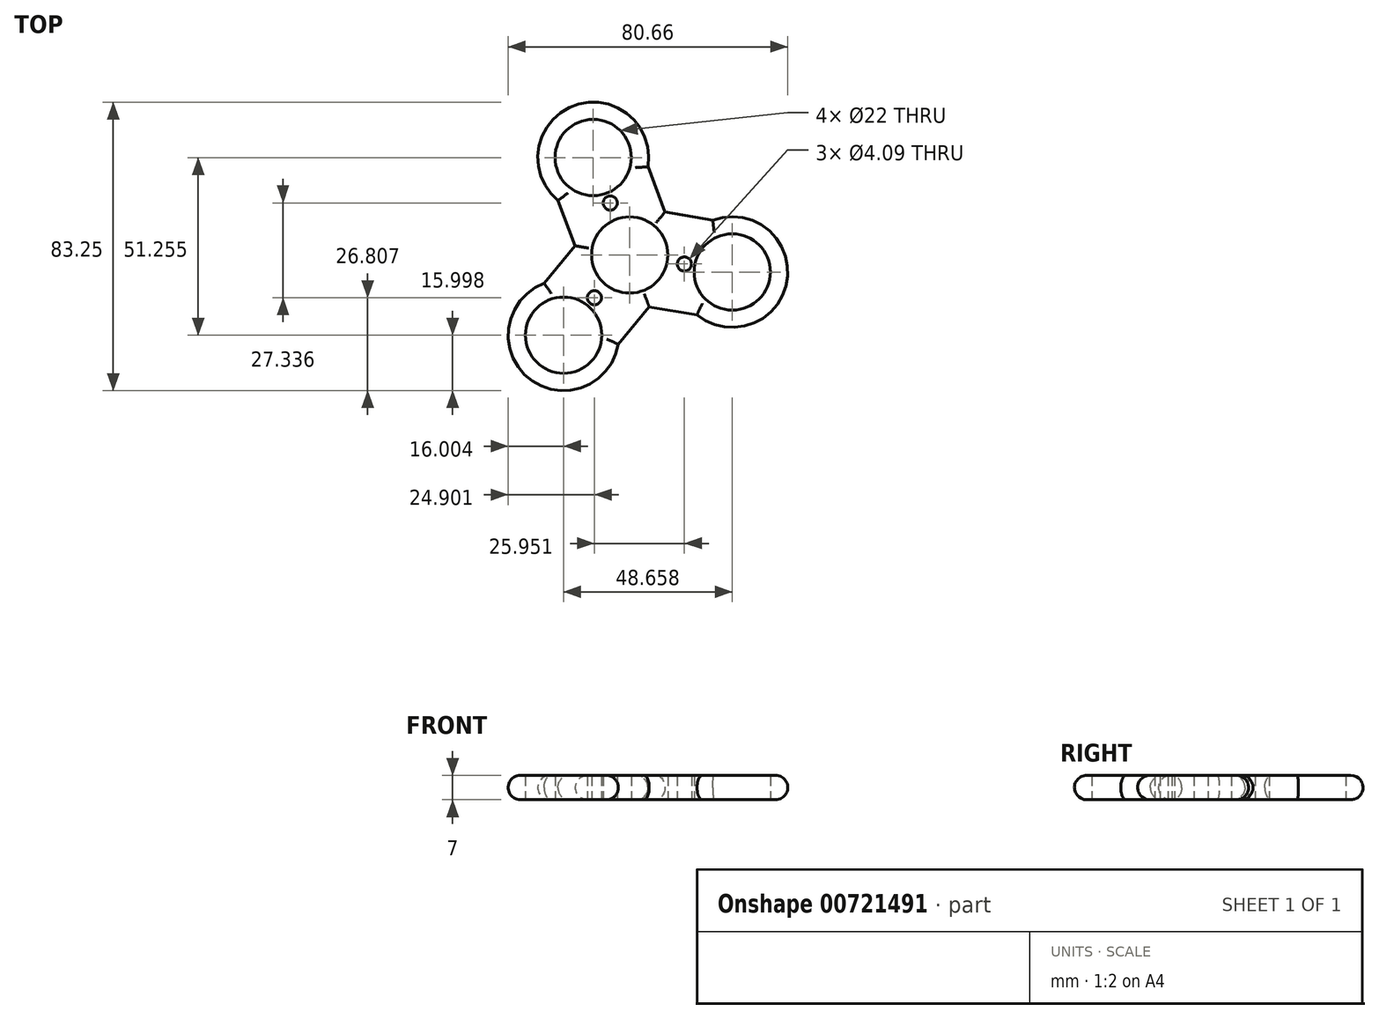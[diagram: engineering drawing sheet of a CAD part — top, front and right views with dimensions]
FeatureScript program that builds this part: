
annotation { "Feature Type Name" : "Feature", "Feature Type Description" : "" }
export const myFeature = defineFeature(function(context is Context, id is Id, definition is map)
    precondition{}
    {
        {
            var Q0;
            Q0=qCreatedBy(makeId("Top.planeOp"),FACE);
            var sketch = newSketch(context, id + "F0", { "sketchPlane" : qUnion([Q0])});
            skCircle(sketch, "E0", {"center": v(0, 0) * mm, "radius": 11 * mm});
            skLineSegment(sketch, "E1", {"start": v(0, 0) * mm, "end": v(-10.53, 28.1) * mm});
            skLineSegment(sketch, "E2", {"start": v(0, 0) * mm, "end": v(-19.07, -23.16) * mm});
            skLineSegment(sketch, "E3", {"start": v(0, 0) * mm, "end": v(29.6, -4.93) * mm});
            skCircle(sketch, "E4", {"center": v(-10.53, 28.1) * mm, "radius": 11 * mm});
            skCircle(sketch, "E5", {"center": v(29.6, -4.93) * mm, "radius": 11 * mm});
            skCircle(sketch, "E6", {"center": v(-19.07, -23.16) * mm, "radius": 11 * mm});
            skCircle(sketch, "E7", {"center": v(-10.53, 28.1) * mm, "radius": 16 * mm});
            skCircle(sketch, "E8", {"center": v(29.6, -4.93) * mm, "radius": 16 * mm});
            skCircle(sketch, "E9", {"center": v(-19.07, -23.16) * mm, "radius": 16 * mm});
            skCircle(sketch, "E10", {"center": v(0, 0) * mm, "radius": 16 * mm});
            skLineSegment(sketch, "E11", {"start": v(0, 0) * mm, "end": v(-15.78, 2.63) * mm, "construction": true});
            skLineSegment(sketch, "E12", {"start": v(0, 0) * mm, "end": v(10.17, 12.35) * mm, "construction": true});
            skLineSegment(sketch, "E13", {"start": v(-10.53, 28.1) * mm, "end": v(-20.7, 15.74) * mm, "construction": true});
            skLineSegment(sketch, "E14", {"start": v(-10.53, 28.1) * mm, "end": v(5.26, 25.46) * mm});
            skLineSegment(sketch, "E15", {"start": v(10.17, 12.35) * mm, "end": v(5.26, 25.46) * mm});
            skLineSegment(sketch, "E16", {"start": v(-15.78, 2.63) * mm, "end": v(-20.7, 15.74) * mm});
            skLineSegment(sketch, "E17.MirrorCS", {"start": v(5.61, -14.98) * mm, "end": v(19.42, -17.28) * mm});
            skLineSegment(sketch, "E18.MirrorCS", {"start": v(10.17, 12.35) * mm, "end": v(23.98, 10.05) * mm});
            skLineSegment(sketch, "E19.MirrorCS", {"start": v(-15.78, 2.63) * mm, "end": v(-24.68, -8.18) * mm});
            skLineSegment(sketch, "E20.MirrorCS", {"start": v(5.61, -14.98) * mm, "end": v(-3.28, -25.8) * mm});
            skCircle(sketch, "E21", {"center": v(-10.17, -12.35) * mm, "radius": 2.05 * mm});
            skCircle(sketch, "E22.MirrorC", {"center": v(-5.61, 14.98) * mm, "radius": 2.05 * mm});
            skCircle(sketch, "E23.MirrorC", {"center": v(15.78, -2.63) * mm, "radius": 2.05 * mm});
            skSolve(sketch);
        }
        {
            var Q0;
            Q0=makeQuery(id+"F0.imprint","IMPRINT",FACE,{"disambiguationData":[TD([[makeQuery(id+"F0.imprint","IMPRINT",EDGE,{"derivedFrom":sQuery(id+"F0.wireOp",EDGE,"E5")}),-1.0]])]});
            var Q1;
            Q1=makeQuery(id+"F0.imprint","IMPRINT",FACE,{"disambiguationData":[TD([[makeQuery(id+"F0.imprint","IMPRINT",EDGE,{"derivedFrom":sQuery(id+"F0.wireOp",EDGE,"E6")}),-1.0]])]});
            var Q2;
            {var subQ4=sQuery(id+"F0.wireOp",EDGE,"E2");var subQ5=sQuery(id+"F0.wireOp",EDGE,"E0");var subQ6=makeQuery(id+"F0.imprint","INTERSECT",VERTEX,{"derivedFrom":[subQ5,subQ4]});Q2=makeQuery(id+"F0.imprint","IMPRINT",FACE,{"disambiguationData":[TD([[makeQuery(id+"F0.imprint","IMPRINT",EDGE,{"disambiguationData":[TD([[subQ6,1.0]])],"derivedFrom":subQ5}),-1.0]])]});}
            var Q3;
            {var subQ2=sQuery(id+"F0.wireOp",EDGE,"E2");var subQ5=sQuery(id+"F0.wireOp",EDGE,"E0");var subQ8=makeQuery(id+"F0.imprint","INTERSECT",VERTEX,{"derivedFrom":[subQ5,subQ2]});Q3=makeQuery(id+"F0.imprint","IMPRINT",FACE,{"disambiguationData":[TD([[makeQuery(id+"F0.imprint","IMPRINT",EDGE,{"disambiguationData":[TD([[subQ8,-1.0]])],"derivedFrom":subQ5}),-1.0]])]});}
            var Q4;
            {var subQ0=sQuery(id+"F0.wireOp",EDGE,"E1");var subQ1=sQuery(id+"F0.wireOp",EDGE,"E0");var subQ2=makeQuery(id+"F0.imprint","INTERSECT",VERTEX,{"derivedFrom":[subQ1,subQ0]});Q4=makeQuery(id+"F0.imprint","IMPRINT",FACE,{"disambiguationData":[TD([[makeQuery(id+"F0.imprint","IMPRINT",EDGE,{"disambiguationData":[TD([[subQ2,1.0]])],"derivedFrom":subQ1}),-1.0]])]});}
            var Q5;
            {var subQ0=sQuery(id+"F0.wireOp",EDGE,"wNWGQW3L-Wg3f-4ug6-IvEM-VYyaZqjxjgMl");var subQ1=sQuery(id+"F0.wireOp",EDGE,"E20.MirrorCS");var subQ2=makeQuery(id+"F0.imprint","INTERSECT",VERTEX,{"disambiguationData":[OD(0.0)],"derivedFrom":[subQ1,subQ0]});Q5=makeQuery(id+"F0.imprint","IMPRINT",FACE,{"disambiguationData":[TD([[makeQuery(id+"F0.imprint","IMPRINT",EDGE,{"disambiguationData":[TD([[subQ2,-1.0]])],"derivedFrom":subQ1}),1.0]])]});}
            var Q6;
            {var subQ0=sQuery(id+"F0.wireOp",EDGE,"E21");var subQ1=sQuery(id+"F0.wireOp",EDGE,"E9");var subQ2=makeQuery(id+"F0.imprint","INTERSECT",VERTEX,{"disambiguationData":[OD(0.0)],"derivedFrom":[subQ1,subQ0]});Q6=makeQuery(id+"F0.imprint","IMPRINT",FACE,{"disambiguationData":[TD([[makeQuery(id+"F0.imprint","IMPRINT",EDGE,{"disambiguationData":[TD([[subQ2,1.0]])],"derivedFrom":subQ1}),1.0]])]});}
            var Q7;
            {var subQ0=sQuery(id+"F0.wireOp",EDGE,"E21");var subQ1=sQuery(id+"F0.wireOp",EDGE,"E9");var subQ2=makeQuery(id+"F0.imprint","INTERSECT",VERTEX,{"disambiguationData":[OD(1.0)],"derivedFrom":[subQ1,subQ0]});Q7=makeQuery(id+"F0.imprint","IMPRINT",FACE,{"disambiguationData":[TD([[makeQuery(id+"F0.imprint","IMPRINT",EDGE,{"disambiguationData":[TD([[subQ2,-1.0]])],"derivedFrom":subQ1}),1.0]])]});}
            var Q8;
            {var subQ0=sQuery(id+"F0.wireOp",EDGE,"E10");var subQ1=sQuery(id+"F0.wireOp",EDGE,"E8");var subQ2=makeQuery(id+"F0.imprint","INTERSECT",VERTEX,{"disambiguationData":[OD(0.0)],"derivedFrom":[subQ1,subQ0]});Q8=makeQuery(id+"F0.imprint","IMPRINT",FACE,{"disambiguationData":[TD([[makeQuery(id+"F0.imprint","IMPRINT",EDGE,{"disambiguationData":[TD([[subQ2,-1.0]])],"derivedFrom":subQ1}),1.0]])]});}
            var Q9;
            {var subQ0=sQuery(id+"F0.wireOp",EDGE,"E23.MirrorC");var subQ1=sQuery(id+"F0.wireOp",EDGE,"E8");var subQ2=makeQuery(id+"F0.imprint","INTERSECT",VERTEX,{"disambiguationData":[OD(1.0)],"derivedFrom":[subQ1,subQ0]});Q9=makeQuery(id+"F0.imprint","IMPRINT",FACE,{"disambiguationData":[TD([[makeQuery(id+"F0.imprint","IMPRINT",EDGE,{"disambiguationData":[TD([[subQ2,-1.0]])],"derivedFrom":subQ1}),1.0]])]});}
            var Q10;
            {var subQ3=sQuery(id+"F0.wireOp",EDGE,"E22.MirrorC");var subQ8=sQuery(id+"F0.wireOp",EDGE,"E1");var subQ11=makeQuery(id+"F0.imprint","INTERSECT",VERTEX,{"disambiguationData":[OD(1.0)],"derivedFrom":[subQ8,subQ3]});Q10=makeQuery(id+"F0.imprint","IMPRINT",FACE,{"disambiguationData":[TD([[makeQuery(id+"F0.imprint","IMPRINT",EDGE,{"disambiguationData":[TD([[subQ11,-1.0]])],"derivedFrom":subQ8}),-1.0]])]});}
            var Q11;
            {var subQ4=sQuery(id+"F0.wireOp",EDGE,"E22.MirrorC");var subQ5=sQuery(id+"F0.wireOp",EDGE,"E1");var subQ6=makeQuery(id+"F0.imprint","INTERSECT",VERTEX,{"disambiguationData":[OD(1.0)],"derivedFrom":[subQ5,subQ4]});Q11=makeQuery(id+"F0.imprint","IMPRINT",FACE,{"disambiguationData":[TD([[makeQuery(id+"F0.imprint","IMPRINT",EDGE,{"disambiguationData":[TD([[subQ6,-1.0]])],"derivedFrom":subQ5}),1.0]])]});}
            var Q12;
            {var subQ0=sQuery(id+"F0.wireOp",EDGE,"E22.MirrorC");var subQ1=sQuery(id+"F0.wireOp",EDGE,"E7");var subQ2=makeQuery(id+"F0.imprint","INTERSECT",VERTEX,{"disambiguationData":[OD(1.0)],"derivedFrom":[subQ1,subQ0]});Q12=makeQuery(id+"F0.imprint","IMPRINT",FACE,{"disambiguationData":[TD([[makeQuery(id+"F0.imprint","IMPRINT",EDGE,{"disambiguationData":[TD([[subQ2,-1.0]])],"derivedFrom":subQ1}),1.0]])]});}
            var Q13;
            {var subQ0=sQuery(id+"F0.wireOp",EDGE,"E10");var subQ1=sQuery(id+"F0.wireOp",EDGE,"E7");var subQ2=makeQuery(id+"F0.imprint","INTERSECT",VERTEX,{"disambiguationData":[OD(0.0)],"derivedFrom":[subQ1,subQ0]});Q13=makeQuery(id+"F0.imprint","IMPRINT",FACE,{"disambiguationData":[TD([[makeQuery(id+"F0.imprint","IMPRINT",EDGE,{"disambiguationData":[TD([[subQ2,-1.0]])],"derivedFrom":subQ1}),1.0]])]});}
            var Q14;
            {var subQ1=sQuery(id+"F0.wireOp",EDGE,"e612f9c1-c014-4065-8786-90dc7a8c4ea60.MirrorCS");Q14=makeQuery(id+"F0.imprint","IMPRINT",FACE,{"disambiguationData":[TD([[makeQuery(id+"F0.imprint","IMPRINT",EDGE,{"derivedFrom":subQ1}),1.0]])]});}
            var Q15;
            {var subQ5=sQuery(id+"F0.wireOp",EDGE,"E14");var subQ7=sQuery(id+"F0.wireOp",EDGE,"E4");var subQ8=makeQuery(id+"F0.imprint","INTERSECT",VERTEX,{"derivedFrom":[subQ7,subQ5]});Q15=makeQuery(id+"F0.imprint","IMPRINT",FACE,{"disambiguationData":[TD([[makeQuery(id+"F0.imprint","IMPRINT",EDGE,{"disambiguationData":[TD([[subQ8,1.0]])],"derivedFrom":subQ7}),-1.0]])]});}
            var Q16;
            {var subQ5=sQuery(id+"F0.wireOp",EDGE,"E14");var subQ9=sQuery(id+"F0.wireOp",EDGE,"E4");var subQ12=makeQuery(id+"F0.imprint","INTERSECT",VERTEX,{"derivedFrom":[subQ9,subQ5]});Q16=makeQuery(id+"F0.imprint","IMPRINT",FACE,{"disambiguationData":[TD([[makeQuery(id+"F0.imprint","IMPRINT",EDGE,{"disambiguationData":[TD([[subQ12,-1.0]])],"derivedFrom":subQ9}),-1.0]])]});}
            var Q17;
            {var subQ0=sQuery(id+"F0.wireOp",EDGE,"32d44365-9099-444c-8909-6f45dbab55cc0.MirrorCS");Q17=makeQuery(id+"F0.imprint","IMPRINT",FACE,{"disambiguationData":[TD([[makeQuery(id+"F0.imprint","IMPRINT",EDGE,{"derivedFrom":subQ0}),-1.0]])]});}
            var Q18;
            {var subQ0=sQuery(id+"F0.wireOp",EDGE,"ae01513f-205a-4772-8993-a33fd46c5e690.MirrorCS");Q18=makeQuery(id+"F0.imprint","IMPRINT",FACE,{"disambiguationData":[TD([[makeQuery(id+"F0.imprint","IMPRINT",EDGE,{"derivedFrom":subQ0}),1.0]])]});}
            var Q19;
            {var subQ0=sQuery(id+"F0.wireOp",EDGE,"c8ff0e85-610d-4f0e-9ecb-1ba7e22bc6e30.MirrorCS");Q19=makeQuery(id+"F0.imprint","IMPRINT",FACE,{"disambiguationData":[TD([[makeQuery(id+"F0.imprint","IMPRINT",EDGE,{"derivedFrom":subQ0}),-1.0]])]});}
            var Q20;
            {var subQ1=sQuery(id+"F0.wireOp",EDGE,"91903ac2-48b2-40ea-bbcb-57abc5b5aab90.MirrorCS");Q20=makeQuery(id+"F0.imprint","IMPRINT",FACE,{"disambiguationData":[TD([[makeQuery(id+"F0.imprint","IMPRINT",EDGE,{"derivedFrom":subQ1}),-1.0]])]});}
            var Q21;
            Q21=makeQuery(id+"F0.imprint","IMPRINT",FACE,{"disambiguationData":[TD([[makeQuery(id+"F0.imprint","IMPRINT",EDGE,{"derivedFrom":sQuery(id+"F0.wireOp",EDGE,"E17.MirrorCS")}),1.0]])]});
            var Q22;
            {var subQ0=sQuery(id+"F0.wireOp",EDGE,"8dce575f-2467-473e-b586-ea05cfbc66d80.MirrorCS");Q22=makeQuery(id+"F0.imprint","IMPRINT",FACE,{"disambiguationData":[TD([[makeQuery(id+"F0.imprint","IMPRINT",EDGE,{"derivedFrom":subQ0}),1.0]])]});}
            var Q23;
            Q23=makeQuery(id+"F0.imprint","IMPRINT",FACE,{"disambiguationData":[TD([[makeQuery(id+"F0.imprint","IMPRINT",EDGE,{"derivedFrom":sQuery(id+"F0.wireOp",EDGE,"E20.MirrorCS")}),-1.0]])]});
            var Q24;
            Q24=makeQuery(id+"F0.imprint","IMPRINT",FACE,{"disambiguationData":[TD([[makeQuery(id+"F0.imprint","IMPRINT",EDGE,{"derivedFrom":sQuery(id+"F0.wireOp",EDGE,"E19.MirrorCS")}),1.0]])]});
            var Q25;
            Q25=makeQuery(id+"F0.imprint","IMPRINT",FACE,{"disambiguationData":[TD([[makeQuery(id+"F0.imprint","IMPRINT",EDGE,{"derivedFrom":sQuery(id+"F0.wireOp",EDGE,"E16")}),-1.0]])]});
            var Q26;
            Q26=makeQuery(id+"F0.imprint","IMPRINT",FACE,{"disambiguationData":[TD([[makeQuery(id+"F0.imprint","IMPRINT",EDGE,{"derivedFrom":sQuery(id+"F0.wireOp",EDGE,"E18.MirrorCS")}),-1.0]])]});
            var Q27;
            Q27=makeQuery(id+"F0.imprint","IMPRINT",FACE,{"disambiguationData":[TD([[makeQuery(id+"F0.imprint","IMPRINT",EDGE,{"derivedFrom":sQuery(id+"F0.wireOp",EDGE,"E15")}),1.0]])]});
            extrude(context, id + "F1", {"entities" : qUnion([Q0, Q1, Q2, Q3, Q4, Q5, Q6, Q7, Q8, Q9, Q10, Q11, Q12, Q13, Q14, Q15, Q16, Q17, Q18, Q19, Q20, Q21, Q22, Q23, Q24, Q25, Q26, Q27]), "depth" : 7 * mm, "offsetDistance" : 25 * mm});
        }
        {
            var Q0;
            Q0=makeQuery(id+"F1.opExtrude","CAP_EDGE",EDGE,{"disambiguationData":[OSD([sQuery(id+"F0.wireOp",EDGE,"E9")])],"isStart":true});
            var Q1;
            Q1=makeQuery(id+"F1.opExtrude","CAP_EDGE",EDGE,{"disambiguationData":[OSD([sQuery(id+"F0.wireOp",EDGE,"E19.MirrorCS")])],"isStart":true});
            var Q2;
            Q2=makeQuery(id+"F1.opExtrude","CAP_EDGE",EDGE,{"disambiguationData":[OSD([sQuery(id+"F0.wireOp",EDGE,"E20.MirrorCS")])],"isStart":true});
            var Q3;
            Q3=makeQuery(id+"F1.opExtrude","CAP_EDGE",EDGE,{"disambiguationData":[OSD([sQuery(id+"F0.wireOp",EDGE,"E17.MirrorCS")])],"isStart":true});
            var Q4;
            Q4=makeQuery(id+"F1.opExtrude","CAP_EDGE",EDGE,{"disambiguationData":[OSD([sQuery(id+"F0.wireOp",EDGE,"E8")])],"isStart":true});
            var Q5;
            Q5=makeQuery(id+"F1.opExtrude","CAP_EDGE",EDGE,{"disambiguationData":[OSD([sQuery(id+"F0.wireOp",EDGE,"E18.MirrorCS")])],"isStart":true});
            var Q6;
            Q6=makeQuery(id+"F1.opExtrude","CAP_EDGE",EDGE,{"disambiguationData":[OSD([sQuery(id+"F0.wireOp",EDGE,"E15")])],"isStart":true});
            var Q7;
            Q7=makeQuery(id+"F1.opExtrude","CAP_EDGE",EDGE,{"disambiguationData":[OSD([sQuery(id+"F0.wireOp",EDGE,"E16")])],"isStart":true});
            var Q8;
            Q8=makeQuery(id+"F1.opExtrude","CAP_EDGE",EDGE,{"disambiguationData":[OSD([sQuery(id+"F0.wireOp",EDGE,"E7")])],"isStart":true});
            var Q9;
            Q9=makeQuery(id+"F1.opExtrude","CAP_EDGE",EDGE,{"disambiguationData":[OSD([sQuery(id+"F0.wireOp",EDGE,"E9")])],"isStart":false});
            var Q10;
            Q10=makeQuery(id+"F1.opExtrude","CAP_EDGE",EDGE,{"disambiguationData":[OSD([sQuery(id+"F0.wireOp",EDGE,"E19.MirrorCS")])],"isStart":false});
            var Q11;
            Q11=makeQuery(id+"F1.opExtrude","CAP_EDGE",EDGE,{"disambiguationData":[OSD([sQuery(id+"F0.wireOp",EDGE,"E20.MirrorCS")])],"isStart":false});
            var Q12;
            Q12=makeQuery(id+"F1.opExtrude","CAP_EDGE",EDGE,{"disambiguationData":[OSD([sQuery(id+"F0.wireOp",EDGE,"E17.MirrorCS")])],"isStart":false});
            var Q13;
            Q13=makeQuery(id+"F1.opExtrude","CAP_EDGE",EDGE,{"disambiguationData":[OSD([sQuery(id+"F0.wireOp",EDGE,"E18.MirrorCS")])],"isStart":false});
            var Q14;
            Q14=makeQuery(id+"F1.opExtrude","CAP_EDGE",EDGE,{"disambiguationData":[OSD([sQuery(id+"F0.wireOp",EDGE,"E8")])],"isStart":false});
            var Q15;
            Q15=makeQuery(id+"F1.opExtrude","CAP_EDGE",EDGE,{"disambiguationData":[OSD([sQuery(id+"F0.wireOp",EDGE,"E15")])],"isStart":false});
            var Q16;
            Q16=makeQuery(id+"F1.opExtrude","CAP_EDGE",EDGE,{"disambiguationData":[OSD([sQuery(id+"F0.wireOp",EDGE,"E16")])],"isStart":false});
            var Q17;
            Q17=makeQuery(id+"F1.opExtrude","CAP_EDGE",EDGE,{"disambiguationData":[OSD([sQuery(id+"F0.wireOp",EDGE,"E7")])],"isStart":false});
            var Q18;
            Q18=makeQuery(id+"F1.opExtrude","CAP_EDGE",EDGE,{"disambiguationData":[OSD([sQuery(id+"F0.wireOp",EDGE,"e612f9c1-c014-4065-8786-90dc7a8c4ea60.MirrorCS")])],"isStart":false});
            var Q19;
            Q19=makeQuery(id+"F1.opExtrude","CAP_EDGE",EDGE,{"disambiguationData":[OSD([sQuery(id+"F0.wireOp",EDGE,"c8ff0e85-610d-4f0e-9ecb-1ba7e22bc6e30.MirrorCS")])],"isStart":false});
            var Q20;
            Q20=makeQuery(id+"F1.opExtrude","CAP_EDGE",EDGE,{"disambiguationData":[OSD([sQuery(id+"F0.wireOp",EDGE,"32d44365-9099-444c-8909-6f45dbab55cc0.MirrorCS")])],"isStart":false});
            var Q21;
            Q21=makeQuery(id+"F1.opExtrude","CAP_EDGE",EDGE,{"disambiguationData":[OSD([sQuery(id+"F0.wireOp",EDGE,"ae01513f-205a-4772-8993-a33fd46c5e690.MirrorCS")])],"isStart":false});
            fillet(context, id + "F2", {"entities" : qUnion([Q0, Q1, Q2, Q3, Q4, Q5, Q6, Q7, Q8, Q9, Q10, Q11, Q12, Q13, Q14, Q15, Q16, Q17, Q18, Q19, Q20, Q21]), "radius" : 3.5 * mm, "tangentPropagation" : true, "allowEdgeOverflow" : false});
        }
    });
